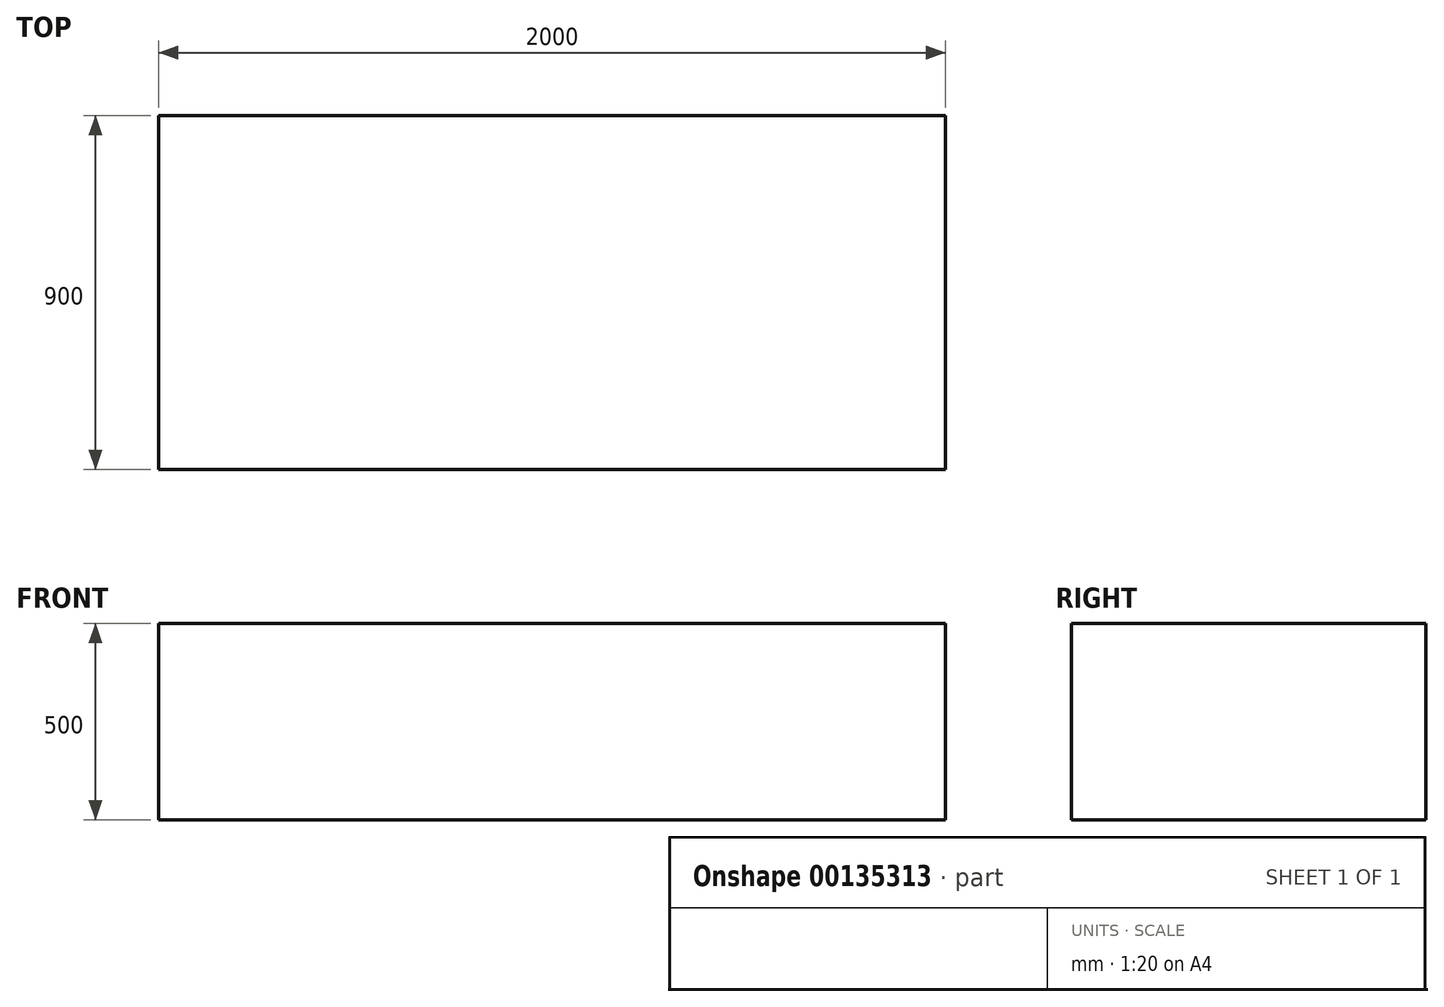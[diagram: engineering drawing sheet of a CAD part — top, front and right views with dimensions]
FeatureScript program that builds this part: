
annotation { "Feature Type Name" : "Feature", "Feature Type Description" : "" }
export const myFeature = defineFeature(function(context is Context, id is Id, definition is map)
    precondition{}
    {
        {
            var Q0;
            Q0=qCreatedBy(makeId("Top.planeOp"),FACE);
            var sketch = newSketch(context, id + "F0", { "sketchPlane" : qUnion([Q0])});
            skLineSegment(sketch, "E0.bottom", {"start": v(-1000, 450) * mm, "end": v(1000, 450) * mm});
            skLineSegment(sketch, "E0.top", {"start": v(-1000, -450) * mm, "end": v(1000, -450) * mm});
            skLineSegment(sketch, "E0.left", {"start": v(-1000, 450) * mm, "end": v(-1000, -450) * mm});
            skLineSegment(sketch, "E0.right", {"start": v(1000, 450) * mm, "end": v(1000, -450) * mm});
            skPoint(sketch, "E0.middle", {"position": v(0, 0) * mm});
            skSolve(sketch);
        }
        {
            var Q0;
            Q0 = qSketchRegion(id + "F0", true);
            extrude(context, id + "F1", {"entities" : qUnion([Q0]), "depth" : 500 * mm});
        }
    });
